# Revit family: GR_Адаптер линейный_Муфта(1)_VL-V-КСД-У-П_R21
name_source: partatom
category: Соединительные детали воздуховодов
units: mm (PartAtom-declared; Revit-internal decimal feet)

## family parameters
Всегда вертикально = Да
Заголовок OmniClass = Metal Ducts
На основе рабочей плоскости = Нет
Номер OmniClass = 23.75.70.14.31
Общий = Нет
При загрузке вырезать с полостями = Нет
Размер круглого соединителя = Использовать диаметр
Тип детали = Мультипорт

## types (15) — shared parameters
ADSK_URL страницы изделия = https://grilles.ru
ADSK_Версия Revit = 2021
ADSK_Единица измерения = шт.
ADSK_Завод-изготовитель = ООО "ВЕНТРЕШЕТКИКОМ"
ADSK_Код изделия = 000157
ADSK_Количество = 1
ADSK_Материал = ADSK_Оцинкованная сталь
ADSK_Наименование = VL-V-КСД-У-П, адаптер вентиляционной решётки
Изготовитель = ООО "ВЕНТРЕШЕТКИКОМ"
Корпус_Металл_Толщина = 1 мм
Муфта_Металл_Толщина = 1 мм
zero-valued in all types: Отметка по умолчанию

## per-type parameters (varying)
| type | Корпус_Высота | Корпус_Длина | Муфта_Отступ_ОВ_2 | Решетка_отступ | Решётка_Высота |
| VL-V-КСД-У-П 1-20 | 75 мм | 166 мм | 83 мм | 24 мм | 46 мм |
| VL-V-КСД-У-П 1-30 | 75 мм | 176 мм | 88 мм | 29 мм | 56 мм |
| VL-V-КСД-У-П 1-40 | 105 мм | 186 мм | 93 мм | 34 мм | 66 мм |
| VL-V-КСД-У-П 1-50 | 105 мм | 196 мм | 98 мм | 39 мм | 76 мм |
| VL-V-КСД-У-П 1-60 | 140 мм | 206 мм | 103 мм | 44 мм | 86 мм |
| VL-V-КСД-У-П 1-70 | 140 мм | 216 мм | 108 мм | 49 мм | 96 мм |
| VL-V-КСД-У-П 2-20 | 105 мм | 206 мм | 103 мм | 44 мм | 86 мм |
| VL-V-КСД-У-П 2-25 | 105 мм | 216 мм | 108 мм | 49 мм | 96 мм |
| VL-V-КСД-У-П 2-30 | 105 мм | 226 мм | 113 мм | 54 мм | 106 мм |
| VL-V-КСД-У-П 3-20 | 105 мм | 246 мм | 123 мм | 64 мм | 126 мм |
| VL-V-КСД-У-П 3-25 | 105 мм | 261 мм | 131 мм | 72 мм | 141 мм |
| VL-V-КСД-У-П 3-30 | 105 мм | 276 мм | 138 мм | 79 мм | 156 мм |
| VL-V-КСД-У-П 4-20 | 140 мм | 286 мм | 143 мм | 84 мм | 166 мм |
| VL-V-КСД-У-П 4-25 | 140 мм | 306 мм | 153 мм | 94 мм | 186 мм |
| VL-V-КСД-У-П 4-30 | 140 мм | 326 мм | 163 мм | 104 мм | 206 мм |

note: column(s) folded — value = type name in every type: ADSK_Марка
